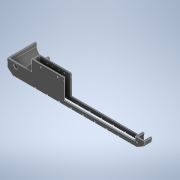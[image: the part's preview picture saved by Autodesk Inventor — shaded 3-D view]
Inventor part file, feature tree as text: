
AUTODESK INVENTOR PART (.ipt)
format: ipt  version: 2022 (Build 260153000, 153)  size: 700,928 bytes
history: native  units: mm
features: sketch x26, extrude x25, chamfer x2, fillet x2
ambient origin geometry x8: Origin, YZ Plane, XZ Plane, XY Plane, X Axis, Y Axis, Z Axis, Center Point
bodies: Solid1 (feature_tree)
feature tree (55):
  extrude  "Extrusion1"  Depth=247.347mm
  extrude  "Extrusion2"  Depth=38.0143mm TaperAngle=0.0deg
  extrude  "Extrusion3"  Depth=2.0mm
  extrude  "Extrusion4"  Depth=8.0mm
  extrude  "Extrusion5"  Depth=1.0mm
  chamfer  "Chamfer1"  [1 undecoded]
  extrude  "Extrusion6"  Depth=2.0mm
  extrude  "Extrusion7"  TaperAngle=0.0deg  [1 undecoded]
  extrude  "Extrusion8"  Depth=3.0mm TaperAngle=45.0deg
  fillet  "Fillet1"  Radius=25.5mm
  fillet  "Fillet2"  Radius=3.0mm
  sketch  "Sketch9"  dims[d23=13.8mm]
  extrude  "Extrusion9"  Depth=48.0mm
  extrude  "Extrusion10"  Depth=5.0mm
  extrude  "Extrusion12"  Depth=12.535mm
  extrude  "Extrusion13"  Depth=1.0mm
  extrude  "Extrusion14"  Depth=2.0mm
  extrude  "Extrusion15"  Depth=35.0mm
  extrude  "Extrusion16"  Depth=11.65mm
  extrude  "Extrusion17"  Depth=6.0mm
  extrude  "Extrusion18"  Depth=5.0mm
  extrude  "Extrusion19"  Depth=20.0mm
  extrude  "Extrusion20"  Depth=20.0mm
  extrude  "Extrusion21"  Depth=10.0mm
  extrude  "Extrusion22"  Depth=2.0mm
  chamfer  "Chamfer2"  Distance=10.0mm
  extrude  "Extrusion23"  Depth=2.0mm
  extrude  "Extrusion24"  Depth=38.5mm TaperAngle=0.0deg
  extrude  "Extrusion25"  Depth=20.0mm
  extrude  "Extrusion26"  Depth=2.0mm TaperAngle=0.0deg
  sketch  "Sketch1"  dims[d0=100.0mm d1=247.347mm]
  sketch  "Sketch2"  dims[d2=100.0mm d3=38.0143mm d4=0.0mm]
  sketch  "Sketch3"  dims[d5=3.5mm d9=2.0mm]
  sketch  "Sketch4"  dims[d12=8.0mm d13=12.5mm]
  sketch  "Sketch5"  dims[d14=6.981317mm d17=1.0mm]
  sketch  "Sketch6"  dims[d20=16.4144mm]
  sketch  "Sketch7"  dims[d21=13.8mm]
  sketch  "Sketch8"  dims[d22=30.0deg]
  sketch  "Sketch10"  dims[d24=19.1mm]
  sketch  "Sketch11"  dims[d26=17.14mm]
  sketch  "Sketch13"  dims[d27=1.5mm]
  sketch  "Sketch14"  dims[d28=2.5mm d29=0.0mm d30=0.0mm]
  sketch  "Sketch15"  dims[d31=2.0mm d32=2.0mm]
  sketch  "Sketch16"  dims[d33=34.5143mm d34=0.0mm d35=0.0mm d36=0.0mm]
  sketch  "Sketch17"  dims[d37=0.0mm d38=0.0mm d39=245.847mm d40=12.197mm d41=45.0deg d42=25.5mm d43=3.0mm]
  sketch  "Sketch18"  dims[d44=0.0mm d45=0.0mm d46=48.0mm]
  sketch  "Sketch19"  dims[d47=5.0mm d48=5.0mm]
  sketch  "Sketch20"  dims[d49=12.535mm d50=0.0mm d51=7.5mm]
  sketch  "Sketch22"  dims[d52=0.0mm d53=0.0mm d54=1.0mm]
  sketch  "Sketch23"  dims[d55=2.0mm d56=37.0mm]
  sketch  "Sketch24"  dims[d59=15.0mm d60=35.0mm]
  sketch  "Sketch25"  dims[d61=2.2mm d62=11.65mm]
  sketch  "Sketch26"  dims[d66=18.4mm d68=6.0mm]
  sketch  "Sketch27"  dims[d69=5.0mm d70=6.0mm]
  sketch  "Sketch28"  dims[d71=10.0mm d73=21.0mm d74=2.2mm d77=10.0mm d78=2.0mm d79=10.0mm d80=2.0mm d81=38.5mm d82=0.0mm d83=5.15mm d84=2.0mm d85=0.0mm d95=14.0mm d96=0.0mm d102=38.5mm d103=0.0mm d104=1.0mm d105=7.0mm d106=1.0mm d109=10.0mm d110=37.05mm d111=6.0mm d112=10.0mm d113=2.2mm d116=2.2mm d119=2.2mm d122=2.2mm d125=2.2mm d128=2.2mm d131=11.95mm d132=30.05mm d133=11.95mm d134=30.05mm d135=11.95mm d136=30.05mm d137=7.0mm d142=2.0mm d143=10.0mm d144=6.0mm d145=21.0mm d146=30.05mm d147=11.95mm d148=30.05mm d149=11.95mm d150=30.05mm d151=11.95mm d152=30.05mm d153=7.0mm d154=38.5mm d155=0.0mm d156=7.0mm d167=7.0mm d168=30.05mm d169=18.4mm d170=41.0mm d171=2.2mm d172=21.0mm d173=21.0mm d174=21.0mm d175=21.0mm d176=21.0mm d177=21.0mm d178=21.0mm d179=15.0mm d180=14.0mm d181=0.0mm d184=2.2mm d185=2.2mm d186=2.2mm d187=2.2mm d188=2.2mm d189=2.2mm d190=2.2mm d191=2.2mm d192=1.0mm d193=10.0mm d194=13.75mm d195=2.2mm d196=30.05mm d197=9.05mm d198=2.2mm d199=30.05mm d200=9.05mm d201=2.2mm d202=2.2mm d203=2.2mm d204=2.2mm d205=2.2mm d206=2.2mm d207=2.2mm d208=2.2mm d209=2.2mm d210=2.2mm d211=2.2mm d212=2.2mm d213=2.2mm d214=2.2mm d215=7.0mm d216=5.0mm d217=1.6mm d218=10.0mm d219=0.0mm d220=10.0mm d221=0.0mm d222=5.0mm d223=7.0mm d224=18.4mm d225=18.4mm d226=9.05mm d227=30.05mm d228=2.2mm d229=11.95mm d230=2.2mm d231=2.2mm d232=2.2mm d233=14.0mm d234=0.0mm d235=7.0mm d236=3.0mm d237=38.5mm d238=0.0mm d239=38.5mm d240=0.0mm d241=15.0mm d242=6.0mm d243=2.2mm d244=0.0mm d245=0.0mm d246=1.5mm d247=2.0mm d248=12.0mm d249=0.0mm d250=5.0mm d251=1.224mm d252=45.0deg d253=0.0mm d254=0.0mm d255=2.2mm d256=2.2mm d257=2.2mm d258=2.2mm d259=2.2mm d260=2.2mm d261=2.2mm d262=70.0mm d263=35.0mm d264=0.0mm d265=2.0mm d266=3.0mm d267=27.0mm d268=0.0mm d269=2.0mm d270=20.0mm d271=0.0mm]
note: 2 required parameter values undecoded (feature->parameter linkage not recoverable at this tier; creation-order binding heuristic only, values carry confidence <= 0.55)
